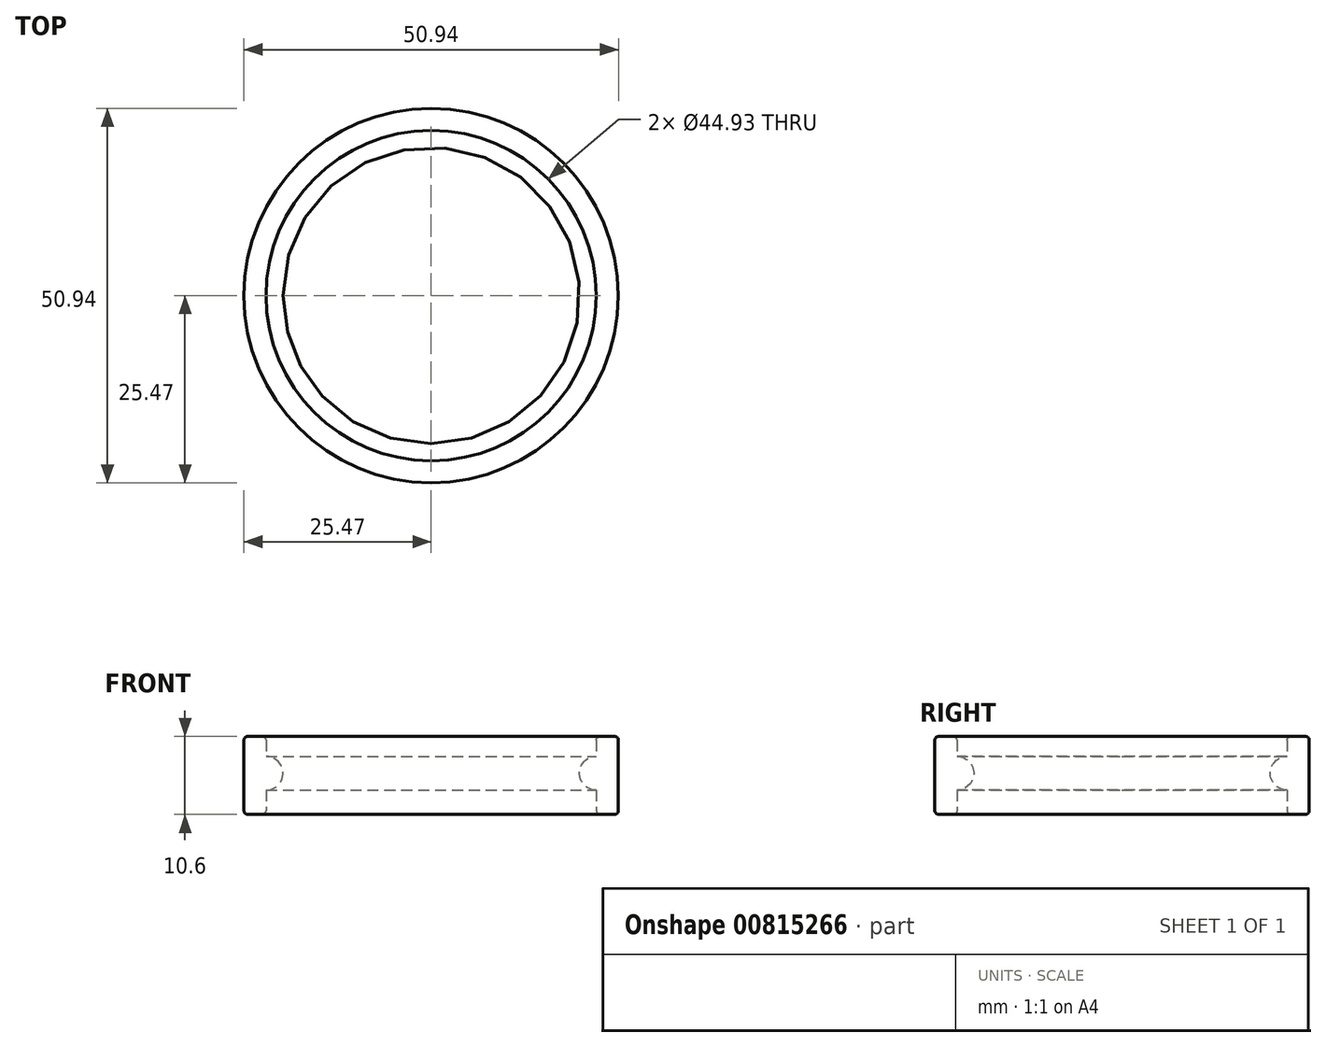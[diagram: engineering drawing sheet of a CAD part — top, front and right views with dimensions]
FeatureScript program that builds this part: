
annotation { "Feature Type Name" : "Feature", "Feature Type Description" : "" }
export const myFeature = defineFeature(function(context is Context, id is Id, definition is map)
    precondition{}
    {
        {
            var Q0;
            Q0=qCreatedBy(makeId("Top.planeOp"),FACE);
            var sketch = newSketch(context, id + "F0", { "sketchPlane" : qUnion([Q0])});
            skCircle(sketch, "E0", {"center": v(0, 0) * mm, "radius": 22.5 * mm});
            skSolve(sketch);
        }
        {
            var Q0;
            Q0=qCreatedBy(makeId("Front.planeOp"),FACE);
            var sketch = newSketch(context, id + "F1", { "sketchPlane" : qUnion([Q0])});
            skArc(sketch, "E1", {"start": v(-22.47, -2.3) * mm, "mid": v(-20.17, 0) * mm, "end": v(-22.47, 2.3) * mm});
            skLineSegment(sketch, "E2.bottom", {"start": v(-24.97, 5) * mm, "end": v(-22.97, 5) * mm});
            skLineSegment(sketch, "E2.top", {"start": v(-24.97, -5.6) * mm, "end": v(-22.97, -5.6) * mm});
            skLineSegment(sketch, "E2.right", {"start": v(-22.47, 4.5) * mm, "end": v(-22.47, -5.1) * mm});
            skLineSegment(sketch, "E3", {"start": v(-25.47, 4.5) * mm, "end": v(-25.47, -5.1) * mm});
            skPoint(sketch, "E4.visualSharp", {"position": v(-25.47, 5) * mm});
            skArc(sketch, "E4.filletArc", {"start": v(-24.97, 5) * mm, "mid": v(-25.32, 4.85) * mm, "end": v(-25.47, 4.5) * mm});
            skArc(sketch, "E5.filletArc", {"start": v(-22.47, 4.5) * mm, "mid": v(-22.61, 4.85) * mm, "end": v(-22.97, 5) * mm});
            skPoint(sketch, "E6.visualSharp", {"position": v(-25.47, -5.6) * mm});
            skArc(sketch, "E6.filletArc", {"start": v(-25.47, -5.1) * mm, "mid": v(-25.32, -5.45) * mm, "end": v(-24.97, -5.6) * mm});
            skPoint(sketch, "E7.visualSharp", {"position": v(-22.47, -5.6) * mm});
            skArc(sketch, "E7.filletArc", {"start": v(-22.97, -5.6) * mm, "mid": v(-22.61, -5.45) * mm, "end": v(-22.47, -5.1) * mm});
            skSolve(sketch);
        }
        {
            var Q0;
            Q0=qSketchRegion(id+"F1",true);
            var Q1;
            Q1=sQuery(id+"F0.wireOp",EDGE,"E0");
            revolve(context, id + "F2", {"surfaceOperationType" : NewSurfaceOperationType.NEW, "entities" : qUnion([Q0]), "axis" : qUnion([Q1]), "revolveType" : RevolveType.FULL});
        }
    });
